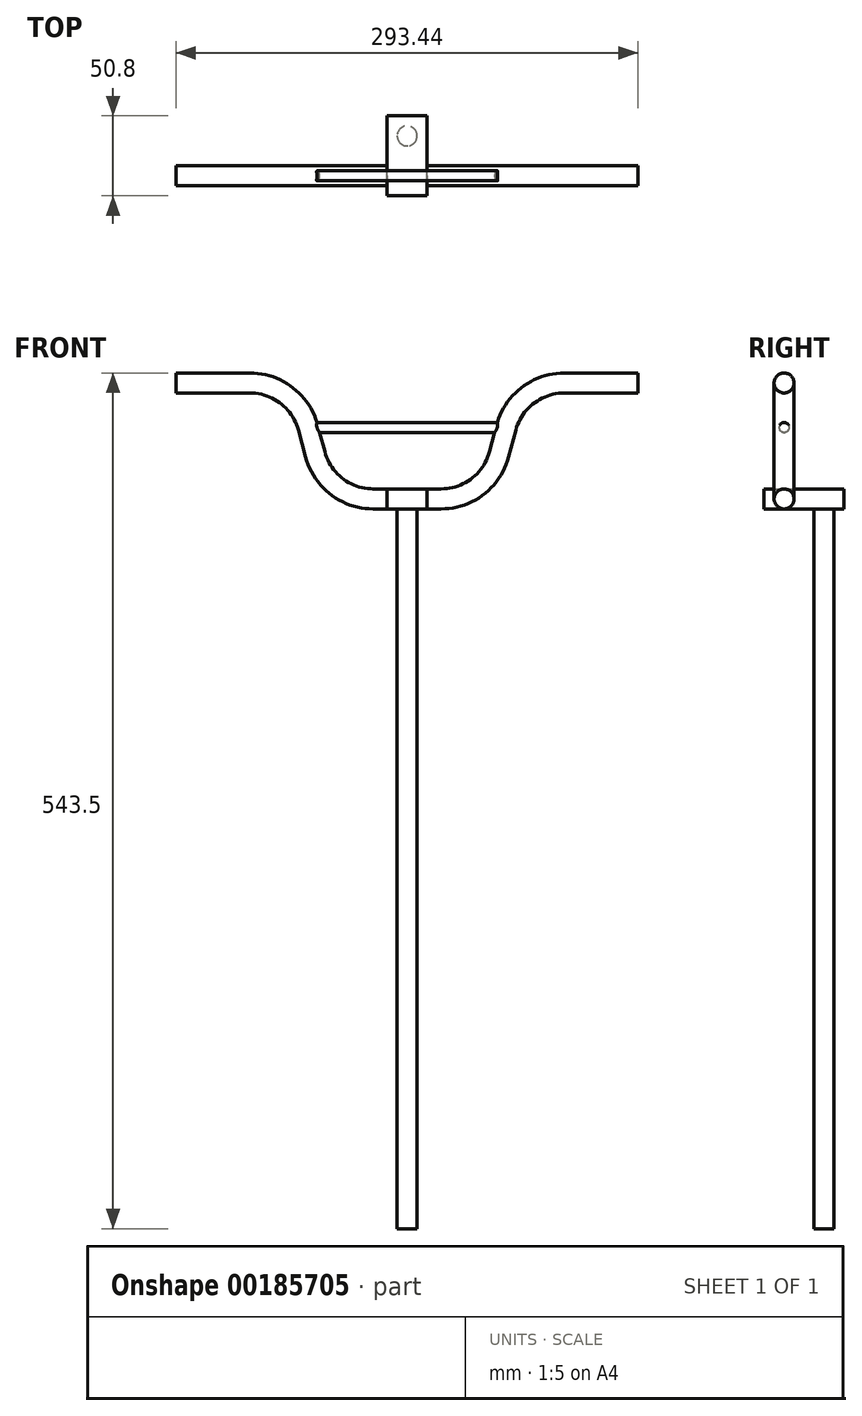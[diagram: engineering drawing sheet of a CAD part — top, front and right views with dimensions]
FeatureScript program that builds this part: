
annotation { "Feature Type Name" : "Feature", "Feature Type Description" : "" }
export const myFeature = defineFeature(function(context is Context, id is Id, definition is map)
    precondition{}
    {
        {
            var Q0;
            Q0=qCreatedBy(makeId("Front.planeOp"),FACE);
            var sketch = newSketch(context, id + "F0", { "sketchPlane" : qUnion([Q0])});
            skLineSegment(sketch, "E0", {"start": v(0, 0) * mm, "end": v(-21.56, 0) * mm});
            skLineSegment(sketch, "E1", {"start": v(-58.37, 28.24) * mm, "end": v(-62.96, 45.36) * mm});
            skLineSegment(sketch, "E2", {"start": v(-99.76, 73.6) * mm, "end": v(-146.72, 73.6) * mm});
            skLineSegment(sketch, "E3", {"start": v(0, 0) * mm, "end": v(0, 48.82) * mm, "construction": true});
            skPoint(sketch, "E4.visualSharp", {"position": v(-50.8, 0) * mm});
            skArc(sketch, "E4.filletArc", {"start": v(-58.37, 28.24) * mm, "mid": v(-44.76, 7.87) * mm, "end": v(-21.56, 0) * mm});
            skPoint(sketch, "E5.visualSharp", {"position": v(-70.52, 73.6) * mm});
            skArc(sketch, "E5.filletArc", {"start": v(-62.96, 45.36) * mm, "mid": v(-76.56, 65.73) * mm, "end": v(-99.76, 73.6) * mm});
            skLineSegment(sketch, "E6.MirrorCS", {"start": v(99.76, 73.6) * mm, "end": v(146.72, 73.6) * mm});
            skArc(sketch, "E7.MirrorCS", {"start": v(62.96, 45.36) * mm, "mid": v(76.56, 65.73) * mm, "end": v(99.76, 73.6) * mm});
            skLineSegment(sketch, "E8.MirrorCS", {"start": v(58.37, 28.24) * mm, "end": v(62.96, 45.36) * mm});
            skArc(sketch, "E9.MirrorCS", {"start": v(58.37, 28.24) * mm, "mid": v(44.76, 7.87) * mm, "end": v(21.56, 0) * mm});
            skLineSegment(sketch, "E10.MirrorCS", {"start": v(0, 0) * mm, "end": v(21.56, 0) * mm});
            skSolve(sketch);
        }
        {
            var Q0;
            Q0=qCreatedBy(makeId("Right.planeOp"),FACE);
            var Q1;
            Q1=sQuery(id+"F0.wireOp",VERTEX,"E6.MirrorCS.end");
            cPlane(context, id + "F1", {"entities" : qUnion([Q0, Q1]), "cplaneType" : CPlaneType.PLANE_POINT, "offset" : 25.4 * mm, "width" : 152.4 * mm, "height" : 152.4 * mm});
        }
        {
            var Q0;
            Q0=qCreatedBy(id+"F1.planeOp",FACE);
            var sketch = newSketch(context, id + "F2", { "sketchPlane" : qUnion([Q0])});
            skCircle(sketch, "E11", {"center": v(0, 73.6) * mm, "radius": 6.35 * mm});
            skSolve(sketch);
        }
        {
            var Q0;
            Q0=qCreatedBy(makeId("Front.planeOp"),FACE);
            var sketch = newSketch(context, id + "F3", { "sketchPlane" : qUnion([Q0])});
            skLineSegment(sketch, "E12", {"start": v(62.96, 45.36) * mm, "end": v(-62.96, 45.36) * mm});
            skSolve(sketch);
        }
        {
            var Q0;
            Q0=qCreatedBy(makeId("Right.planeOp"),FACE);
            var Q1;
            Q1=sQuery(id+"F3.wireOp",VERTEX,"E12.start");
            cPlane(context, id + "F4", {"entities" : qUnion([Q0, Q1]), "cplaneType" : CPlaneType.PLANE_POINT, "offset" : 25.4 * mm, "width" : 152.4 * mm, "height" : 152.4 * mm});
        }
        {
            var Q0;
            Q0=qCreatedBy(id+"F4.planeOp",FACE);
            var sketch = newSketch(context, id + "F5", { "sketchPlane" : qUnion([Q0])});
            skCircle(sketch, "E13", {"center": v(0, 45.36) * mm, "radius": 3.18 * mm});
            skSolve(sketch);
        }
        {
            var Q0;
            Q0=makeQuery(id+"F2.imprint","IMPRINT",FACE,{"disambiguationData":[TD([[makeQuery(id+"F2.imprint","IMPRINT",EDGE,{"derivedFrom":sQuery(id+"F2.wireOp",EDGE,"E11")}),1.0]])]});
            var Q1;
            Q1=sQuery(id+"F0.wireOp",EDGE,"E6.MirrorCS");
            var Q2;
            Q2=sQuery(id+"F0.wireOp",EDGE,"E7.MirrorCS");
            var Q3;
            Q3=sQuery(id+"F0.wireOp",EDGE,"E8.MirrorCS");
            var Q4;
            Q4=sQuery(id+"F0.wireOp",EDGE,"E9.MirrorCS");
            var Q5;
            Q5=sQuery(id+"F0.wireOp",EDGE,"E10.MirrorCS");
            var Q6;
            Q6=sQuery(id+"F0.wireOp",EDGE,"E4.filletArc");
            var Q7;
            Q7=sQuery(id+"F0.wireOp",EDGE,"E0");
            var Q8;
            Q8=sQuery(id+"F0.wireOp",EDGE,"E1");
            var Q9;
            Q9=sQuery(id+"F0.wireOp",EDGE,"E5.filletArc");
            var Q10;
            Q10=sQuery(id+"F0.wireOp",EDGE,"E2");
            sweep(context, id + "F6", {"profiles" : qUnion([Q0]), "path" : qUnion([Q1, Q2, Q3, Q4, Q5, Q6, Q7, Q8, Q9, Q10])});
        }
        {
            var Q0;
            Q0 = qSketchRegion(id + "F5", true);
            var Q1;
            Q1=sQuery(id+"F3.wireOp",EDGE,"E12");
            sweep(context, id + "F7", {"operationType" : NewBodyOperationType.ADD, "profiles" : qUnion([Q0]), "path" : qUnion([Q1])});
        }
        {
            var Q0;
            Q0=qCreatedBy(makeId("Top.planeOp"),FACE);
            var sketch = newSketch(context, id + "F8", { "sketchPlane" : qUnion([Q0])});
            skLineSegment(sketch, "E14.bottom", {"start": v(12.7, -12.7) * mm, "end": v(-12.7, -12.7) * mm});
            skLineSegment(sketch, "E14.top", {"start": v(12.7, 38.1) * mm, "end": v(-12.7, 38.1) * mm});
            skLineSegment(sketch, "E14.left", {"start": v(12.7, -12.7) * mm, "end": v(12.7, 38.1) * mm});
            skLineSegment(sketch, "E14.right", {"start": v(-12.7, -12.7) * mm, "end": v(-12.7, 38.1) * mm});
            skPoint(sketch, "E14.middle", {"position": v(0, 12.7) * mm});
            skSolve(sketch);
        }
        {
            var Q0;
            Q0 = qSketchRegion(id + "F8", true);
            extrude(context, id + "F9", {"entities" : qUnion([Q0]), "operationType" : NewBodyOperationType.ADD, "depth" : 6.35 * mm});
        }
        {
            var Q0;
            Q0 = qSketchRegion(id + "F8", true);
            extrude(context, id + "F10", {"entities" : qUnion([Q0]), "operationType" : NewBodyOperationType.ADD, "oppositeDirection" : true, "depth" : 6.35 * mm});
        }
        {
            var Q0;
            Q0=makeQuery(id+"F10.opExtrude","CAP_FACE",FACE,{"disambiguationData":[OSD([sQuery(id+"F8.wireOp",EDGE,"E14.bottom"),sQuery(id+"F8.wireOp",EDGE,"E14.top"),sQuery(id+"F8.wireOp",EDGE,"E14.left"),sQuery(id+"F8.wireOp",EDGE,"E14.right")])],"isStart":false});
            var sketch = newSketch(context, id + "F11", { "sketchPlane" : qUnion([Q0])});
            skCircle(sketch, "E15", {"center": v(0, -25.4) * mm, "radius": 6.35 * mm});
            skSolve(sketch);
        }
        {
            var Q0;
            Q0=makeQuery(id+"F11.imprint","IMPRINT",FACE,{"disambiguationData":[TD([[makeQuery(id+"F11.imprint","IMPRINT",EDGE,{"derivedFrom":sQuery(id+"F11.wireOp",EDGE,"E15")}),1.0]])]});
            extrude(context, id + "F12", {"entities" : qUnion([Q0]), "operationType" : NewBodyOperationType.ADD, "depth" : 457.2 * mm});
        }
    });
